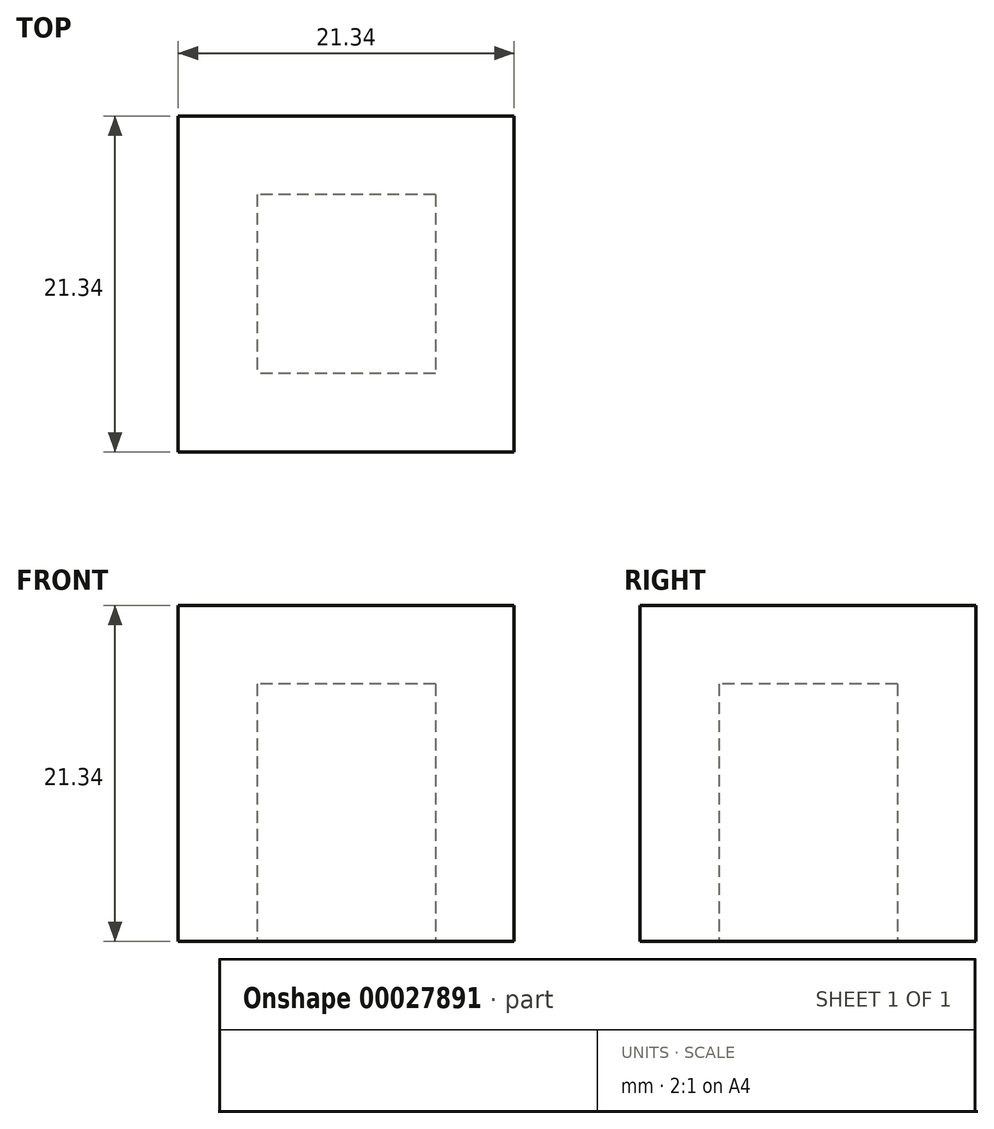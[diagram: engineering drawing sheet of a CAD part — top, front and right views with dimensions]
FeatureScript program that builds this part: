
annotation { "Feature Type Name" : "Feature", "Feature Type Description" : "" }
export const myFeature = defineFeature(function(context is Context, id is Id, definition is map)
    precondition{}
    {
        {
            var Q0;
            Q0=qCreatedBy(makeId("Top.planeOp"),FACE);
            var sketch = newSketch(context, id + "F0", { "sketchPlane" : qUnion([Q0])});
            skLineSegment(sketch, "E0.rect.bottom", {"start": v(10.67, 10.67) * mm, "end": v(-10.67, 10.67) * mm});
            skLineSegment(sketch, "E0.rect.top", {"start": v(10.67, -10.67) * mm, "end": v(-10.67, -10.67) * mm});
            skLineSegment(sketch, "E0.rect.left", {"start": v(10.67, 10.67) * mm, "end": v(10.67, -10.67) * mm});
            skLineSegment(sketch, "E0.rect.right", {"start": v(-10.67, 10.67) * mm, "end": v(-10.67, -10.67) * mm});
            skPoint(sketch, "E0.rect.middle", {"position": v(0, 0) * mm});
            skSolve(sketch);
        }
        {
            var Q0;
            Q0=makeQuery(id+"F0.imprint","IMPRINT",FACE,{"disambiguationData":[TD([[makeQuery(id+"F0.imprint","IMPRINT",EDGE,{"derivedFrom":sQuery(id+"F0.wireOp",EDGE,"E0.rect.bottom")}),1.0]])]});
            extrude(context, id + "F1", {"entities" : qUnion([Q0]), "depth" : 21.34 * mm});
        }
        {
            var Q0;
            Q0=makeQuery(id+"F1.opExtrude","CAP_FACE",FACE,{"disambiguationData":[OSD([sQuery(id+"F0.wireOp",EDGE,"E0.rect.bottom"),sQuery(id+"F0.wireOp",EDGE,"E0.rect.top"),sQuery(id+"F0.wireOp",EDGE,"E0.rect.left"),sQuery(id+"F0.wireOp",EDGE,"E0.rect.right")])],"isStart":true});
            shell(context, id + "F2", {"entities" : qUnion([Q0]), "thickness" : 5 * mm});
        }
    });
